# Revit family: Door_Coiling_Dynaco_Control-Box
name_source: partatom
category: Generic Models
units: mm (PartAtom-declared; Revit-internal decimal feet)

## family parameters
Can host rebar = No
Classification Number = 23.30.10.17.27.11
Cut with Voids When Loaded = No
Host = Face
Maintain Annotation Orientation = No
Part Type = Normal
Room Calculation Point = No
Round Connector Dimension = Use Diameter
Shared = No

## types (1)
- Door_Coiling_Dynaco_Control-Box
    Assembly Code = C1020100
    CAD Details = https://www.arcat.com
    Default Elevation = 0' - 0"
    Description = Dynaco Control Box - Size as Specified
    Keynote = 08 34 00
    Manufacturer = Dynaco/Entrematic
    Model = As Specified
    Product Page URL = https://www.arcat.com
    Specification = http://www.arcat.com
    Type Comments = Contact Dynaco for Size required for your door.
    URL = http://www.dynacodoor.us

## geometry (parser evidence)
native form markers: Sweep x1
no freeform markers — native parametric forms only
